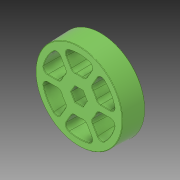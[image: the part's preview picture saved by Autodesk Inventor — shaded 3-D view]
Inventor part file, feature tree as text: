
AUTODESK INVENTOR PART (.ipt)
format: ipt  version: 2018 (Build 220112000, 112)  size: 678,400 bytes
history: native  units: in
note: dims shown in document units (in); Inventor stores cm internally (conversion verified against a paired STEP export)
features: fillet x1
ambient origin geometry x8: Origin, YZ Plane, XZ Plane, XY Plane, X Axis, Y Axis, Z Axis, Center Point
bodies: Solid1 (feature_tree)
feature tree (1):
  fillet  "Fillet3"  [1 undecoded]
note: 1 required parameter value undecoded (feature->parameter linkage not recoverable at this tier; creation-order binding heuristic only, values carry confidence <= 0.55)
